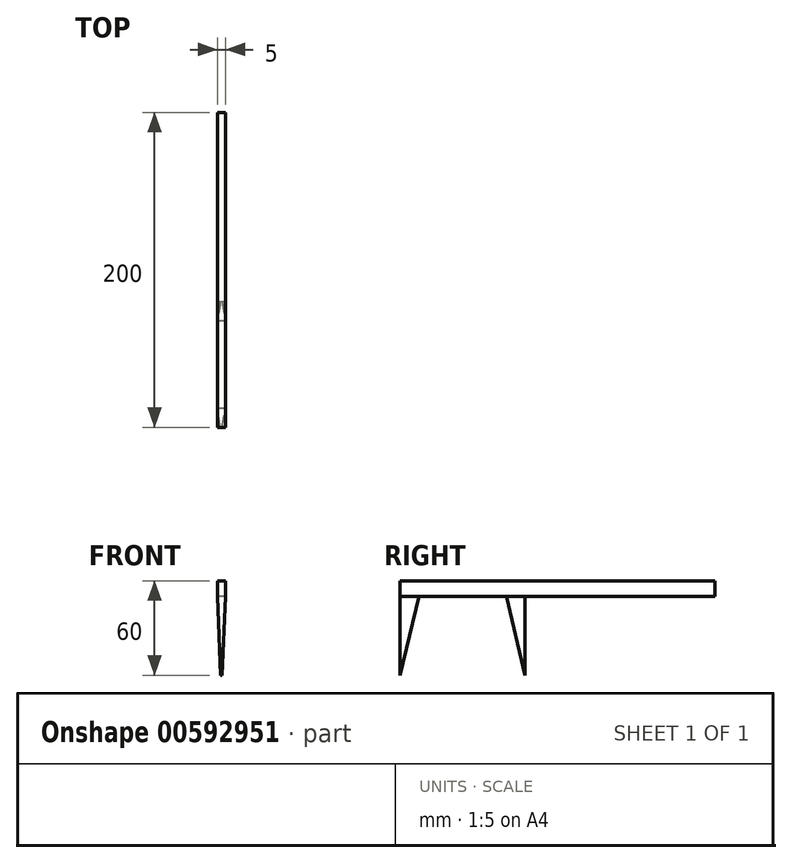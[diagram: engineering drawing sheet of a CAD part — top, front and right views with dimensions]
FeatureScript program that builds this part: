
annotation { "Feature Type Name" : "Feature", "Feature Type Description" : "" }
export const myFeature = defineFeature(function(context is Context, id is Id, definition is map)
    precondition{}
    {
        {
            var Q0;
            Q0=qCreatedBy(makeId("Right.planeOp"),FACE);
            var sketch = newSketch(context, id + "F0", { "sketchPlane" : qUnion([Q0])});
            skLineSegment(sketch, "E0", {"start": v(0, 60) * mm, "end": v(200, 60) * mm});
            skLineSegment(sketch, "E1", {"start": v(200, 60) * mm, "end": v(200, 50) * mm});
            skLineSegment(sketch, "E2", {"start": v(200, 50) * mm, "end": v(79.5, 50) * mm});
            skLineSegment(sketch, "E3", {"start": v(0, 60) * mm, "end": v(0, 0) * mm});
            skLineSegment(sketch, "E4", {"start": v(0, 0) * mm, "end": v(12, 50) * mm});
            skLineSegment(sketch, "E5", {"start": v(79.5, 50) * mm, "end": v(79.5, 0) * mm});
            skLineSegment(sketch, "E6", {"start": v(79.5, 0) * mm, "end": v(67.5, 50) * mm});
            skLineSegment(sketch, "E7.trimOffspring", {"start": v(67.5, 50) * mm, "end": v(12, 50) * mm});
            skSolve(sketch);
        }
        {
            var Q0;
            Q0=makeQuery(id+"F0.imprint","IMPRINT",FACE,{"disambiguationData":[TD([[makeQuery(id+"F0.imprint","IMPRINT",EDGE,{"derivedFrom":sQuery(id+"F0.wireOp",EDGE,"4j12M8s8-po2s-vAIs-Nyqi-q7BRcH3PNNdT")}),-1.0]])]});
            var Q1;
            Q1=makeQuery(id+"F0.imprint","IMPRINT",FACE,{"disambiguationData":[TD([[makeQuery(id+"F0.imprint","IMPRINT",EDGE,{"derivedFrom":sQuery(id+"F0.wireOp",EDGE,"E0")}),-1.0]])]});
            extrude(context, id + "F1", {"entities" : qUnion([Q0, Q1]), "depth" : 5 * mm, "offsetDistance" : 25 * mm});
        }
        {
            var Q0;
            Q0=makeQuery(id+"F1.opExtrude","SWEPT_FACE",FACE,{"disambiguationData":[OSD([sQuery(id+"F0.wireOp",EDGE,"E3")])]});
            var sketch = newSketch(context, id + "F2", { "sketchPlane" : qUnion([Q0])});
            skLineSegment(sketch, "E8", {"start": v(2.5, 0) * mm, "end": v(2.5, 60) * mm, "construction": true});
            skLineSegment(sketch, "E9", {"start": v(0, 50) * mm, "end": v(5, 50) * mm});
            skLineSegment(sketch, "E10", {"start": v(2, 0) * mm, "end": v(0, 50) * mm});
            skLineSegment(sketch, "E11", {"start": v(0, 0) * mm, "end": v(0, 50) * mm});
            skLineSegment(sketch, "E12", {"start": v(0, 0) * mm, "end": v(2, 0) * mm});
            skLineSegment(sketch, "E13", {"start": v(5, 50) * mm, "end": v(5, 0) * mm});
            skLineSegment(sketch, "E14", {"start": v(5, 0) * mm, "end": v(3, 0) * mm});
            skLineSegment(sketch, "E15", {"start": v(3, 0) * mm, "end": v(5, 50) * mm});
            skSolve(sketch);
        }
        {
            var Q0;
            Q0=makeQuery(id+"F2.imprint","IMPRINT",FACE,{"disambiguationData":[TD([[makeQuery(id+"F2.imprint","IMPRINT",EDGE,{"derivedFrom":sQuery(id+"F2.wireOp",EDGE,"E10")}),1.0]])]});
            var Q1;
            Q1=makeQuery(id+"F2.imprint","IMPRINT",FACE,{"disambiguationData":[TD([[makeQuery(id+"F2.imprint","IMPRINT",EDGE,{"derivedFrom":sQuery(id+"F2.wireOp",EDGE,"E13")}),-1.0]])]});
            extrude(context, id + "F3", {"entities" : qUnion([Q0, Q1]), "operationType" : NewBodyOperationType.REMOVE, "endBound" : BoundingType.THROUGH_ALL, "oppositeDirection" : true, "depth" : 25 * mm, "offsetDistance" : 25 * mm});
        }
    });
